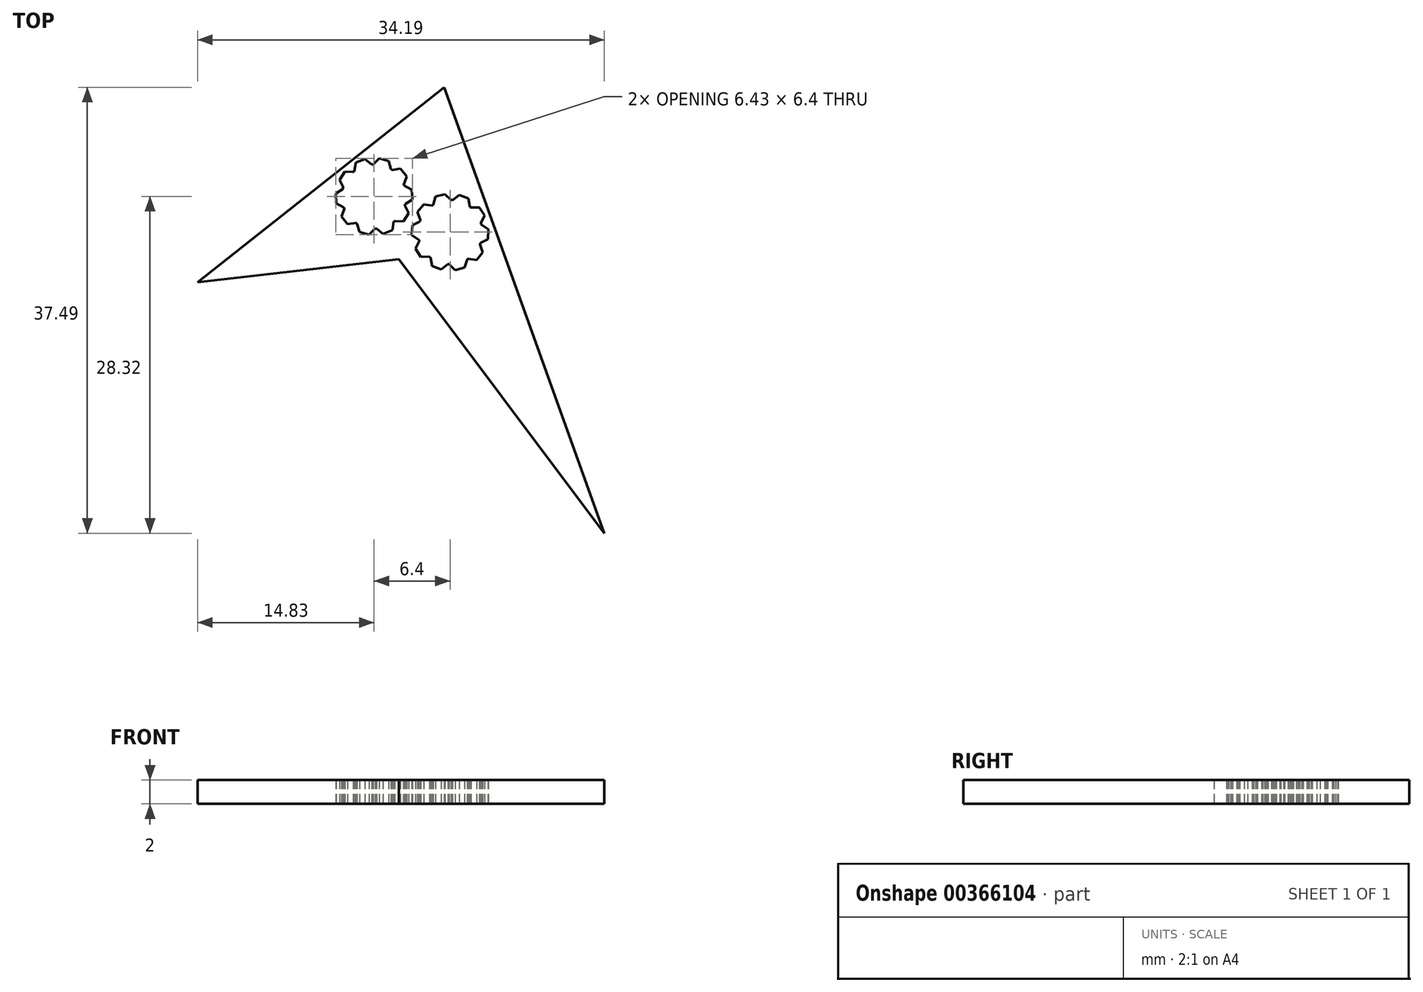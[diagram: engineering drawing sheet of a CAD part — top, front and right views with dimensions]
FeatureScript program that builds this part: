
annotation { "Feature Type Name" : "Feature", "Feature Type Description" : "" }
export const myFeature = defineFeature(function(context is Context, id is Id, definition is map)
    precondition{}
    {
        {
            var Q0;
            Q0=qCreatedBy(makeId("Top.planeOp"),FACE);
            var sketch = newSketch(context, id + "F0", { "sketchPlane" : qUnion([Q0])});
            skLineSegment(sketch, "E0", {"start": v(18, -24) * mm, "end": v(4, 15) * mm});
            skLineSegment(sketch, "E1", {"start": v(4, 15) * mm, "end": v(-17.5, -2) * mm});
            skLineSegment(sketch, "E2", {"start": v(-17.5, -2) * mm, "end": v(0, 0) * mm});
            skLineSegment(sketch, "E3", {"start": v(0, 0) * mm, "end": v(18, -24) * mm});
            skArc(sketch, "E4", {"start": v(-4.38, 6.27) * mm, "mid": v(-4.41, 6.15) * mm, "end": v(-4.45, 6.02) * mm, "construction": true});
            skLineSegment(sketch, "E5", {"start": v(-2, 8) * mm, "end": v(-1.51, 8.48) * mm});
            skLineSegment(sketch, "E6", {"start": v(-1.51, 8.48) * mm, "end": v(-0.93, 8.32) * mm});
            skLineSegment(sketch, "E7", {"start": v(-0.93, 8.32) * mm, "end": v(-0.75, 7.67) * mm});
            skLineSegment(sketch, "E8", {"start": v(-2, 5.5) * mm, "end": v(-1.22, 8.4) * mm, "construction": true});
            skLineSegment(sketch, "E9", {"start": v(-2, 8) * mm, "end": v(-2, 5.5) * mm, "construction": true});
            skLineSegment(sketch, "E10", {"start": v(-2, 5.5) * mm, "end": v(-0.75, 7.67) * mm, "construction": true});
            skLineSegment(sketch, "E11.1.0", {"start": v(-3.47, 7.52) * mm, "end": v(-3.36, 8.2) * mm});
            skLineSegment(sketch, "E11.1.1", {"start": v(-3.36, 8.2) * mm, "end": v(-2.8, 8.4) * mm});
            skLineSegment(sketch, "E11.1.2", {"start": v(-2.8, 8.4) * mm, "end": v(-2.26, 7.99) * mm});
            skLineSegment(sketch, "E11.2.0", {"start": v(-4.38, 6.27) * mm, "end": v(-4.68, 6.88) * mm});
            skLineSegment(sketch, "E11.2.1", {"start": v(-4.68, 6.88) * mm, "end": v(-4.35, 7.39) * mm});
            skLineSegment(sketch, "E11.2.2", {"start": v(-4.35, 7.39) * mm, "end": v(-3.67, 7.36) * mm});
            skLineSegment(sketch, "E11.3.0", {"start": v(-4.38, 4.73) * mm, "end": v(-4.98, 5.04) * mm});
            skLineSegment(sketch, "E11.3.1", {"start": v(-4.98, 5.04) * mm, "end": v(-5.01, 5.64) * mm});
            skLineSegment(sketch, "E11.3.2", {"start": v(-5.01, 5.64) * mm, "end": v(-4.45, 6.02) * mm});
            skLineSegment(sketch, "E11.4.0", {"start": v(-3.47, 3.48) * mm, "end": v(-4.14, 3.38) * mm});
            skLineSegment(sketch, "E11.4.1", {"start": v(-4.14, 3.38) * mm, "end": v(-4.52, 3.85) * mm});
            skLineSegment(sketch, "E11.4.2", {"start": v(-4.52, 3.85) * mm, "end": v(-4.28, 4.48) * mm});
            skLineSegment(sketch, "E11.5.0", {"start": v(-2, 3) * mm, "end": v(-2.49, 2.52) * mm});
            skLineSegment(sketch, "E11.5.1", {"start": v(-2.49, 2.52) * mm, "end": v(-3.07, 2.68) * mm});
            skLineSegment(sketch, "E11.5.2", {"start": v(-3.07, 2.68) * mm, "end": v(-3.25, 3.33) * mm});
            skLineSegment(sketch, "E11.6.0", {"start": v(-0.53, 3.48) * mm, "end": v(-0.64, 2.8) * mm});
            skLineSegment(sketch, "E11.6.1", {"start": v(-0.64, 2.8) * mm, "end": v(-1.2, 2.6) * mm});
            skLineSegment(sketch, "E11.6.2", {"start": v(-1.2, 2.6) * mm, "end": v(-1.74, 3.01) * mm});
            skLineSegment(sketch, "E11.7.0", {"start": v(0.38, 4.73) * mm, "end": v(0.68, 4.12) * mm});
            skLineSegment(sketch, "E11.7.1", {"start": v(0.68, 4.12) * mm, "end": v(0.35, 3.61) * mm});
            skLineSegment(sketch, "E11.7.2", {"start": v(0.35, 3.61) * mm, "end": v(-0.33, 3.64) * mm});
            skLineSegment(sketch, "E11.8.0", {"start": v(0.38, 6.27) * mm, "end": v(0.98, 5.96) * mm});
            skLineSegment(sketch, "E11.8.1", {"start": v(0.98, 5.96) * mm, "end": v(1.01, 5.36) * mm});
            skLineSegment(sketch, "E11.8.2", {"start": v(1.01, 5.36) * mm, "end": v(0.45, 4.98) * mm});
            skLineSegment(sketch, "E11.9.0", {"start": v(-0.53, 7.52) * mm, "end": v(0.14, 7.62) * mm});
            skLineSegment(sketch, "E11.9.1", {"start": v(0.14, 7.62) * mm, "end": v(0.52, 7.15) * mm});
            skLineSegment(sketch, "E11.9.2", {"start": v(0.52, 7.15) * mm, "end": v(0.28, 6.52) * mm});
            skArc(sketch, "E12", {"start": v(2.12, 3.52) * mm, "mid": v(2.07, 3.4) * mm, "end": v(2.02, 3.27) * mm, "construction": true});
            skLineSegment(sketch, "E13", {"start": v(3.15, 4.67) * mm, "end": v(3.33, 5.32) * mm});
            skLineSegment(sketch, "E14", {"start": v(3.33, 5.32) * mm, "end": v(3.91, 5.48) * mm});
            skLineSegment(sketch, "E15", {"start": v(3.91, 5.48) * mm, "end": v(4.4, 5) * mm});
            skLineSegment(sketch, "E16", {"start": v(4.4, 2.5) * mm, "end": v(3.62, 5.4) * mm, "construction": true});
            skLineSegment(sketch, "E17", {"start": v(3.15, 4.67) * mm, "end": v(4.4, 2.5) * mm, "construction": true});
            skLineSegment(sketch, "E18", {"start": v(4.4, 2.5) * mm, "end": v(4.4, 5) * mm, "construction": true});
            skLineSegment(sketch, "E19.1.0", {"start": v(2.12, 3.52) * mm, "end": v(1.88, 4.15) * mm});
            skLineSegment(sketch, "E19.1.1", {"start": v(1.88, 4.15) * mm, "end": v(2.26, 4.62) * mm});
            skLineSegment(sketch, "E19.1.2", {"start": v(2.26, 4.62) * mm, "end": v(2.93, 4.52) * mm});
            skLineSegment(sketch, "E19.2.0", {"start": v(1.95, 1.98) * mm, "end": v(1.39, 2.36) * mm});
            skLineSegment(sketch, "E19.2.1", {"start": v(1.39, 2.36) * mm, "end": v(1.42, 2.96) * mm});
            skLineSegment(sketch, "E19.2.2", {"start": v(1.42, 2.96) * mm, "end": v(2.02, 3.27) * mm});
            skLineSegment(sketch, "E19.3.0", {"start": v(2.73, 0.64) * mm, "end": v(2.05, 0.61) * mm});
            skLineSegment(sketch, "E19.3.1", {"start": v(2.05, 0.61) * mm, "end": v(1.72, 1.12) * mm});
            skLineSegment(sketch, "E19.3.2", {"start": v(1.72, 1.12) * mm, "end": v(2.02, 1.73) * mm});
            skLineSegment(sketch, "E19.4.0", {"start": v(4.14, 0.01) * mm, "end": v(3.6, -0.4) * mm});
            skLineSegment(sketch, "E19.4.1", {"start": v(3.6, -0.4) * mm, "end": v(3.04, -0.2) * mm});
            skLineSegment(sketch, "E19.4.2", {"start": v(3.04, -0.2) * mm, "end": v(2.93, 0.48) * mm});
            skLineSegment(sketch, "E19.5.0", {"start": v(5.65, 0.33) * mm, "end": v(5.47, -0.32) * mm});
            skLineSegment(sketch, "E19.5.1", {"start": v(5.47, -0.32) * mm, "end": v(4.89, -0.48) * mm});
            skLineSegment(sketch, "E19.5.2", {"start": v(4.89, -0.48) * mm, "end": v(4.4, 0) * mm});
            skLineSegment(sketch, "E19.6.0", {"start": v(6.68, 1.48) * mm, "end": v(6.92, 0.85) * mm});
            skLineSegment(sketch, "E19.6.1", {"start": v(6.92, 0.85) * mm, "end": v(6.54, 0.38) * mm});
            skLineSegment(sketch, "E19.6.2", {"start": v(6.54, 0.38) * mm, "end": v(5.87, 0.48) * mm});
            skLineSegment(sketch, "E19.7.0", {"start": v(6.85, 3.02) * mm, "end": v(7.41, 2.64) * mm});
            skLineSegment(sketch, "E19.7.1", {"start": v(7.41, 2.64) * mm, "end": v(7.38, 2.04) * mm});
            skLineSegment(sketch, "E19.7.2", {"start": v(7.38, 2.04) * mm, "end": v(6.78, 1.73) * mm});
            skLineSegment(sketch, "E19.8.0", {"start": v(6.07, 4.36) * mm, "end": v(6.75, 4.39) * mm});
            skLineSegment(sketch, "E19.8.1", {"start": v(6.75, 4.39) * mm, "end": v(7.08, 3.88) * mm});
            skLineSegment(sketch, "E19.8.2", {"start": v(7.08, 3.88) * mm, "end": v(6.78, 3.27) * mm});
            skLineSegment(sketch, "E19.9.0", {"start": v(4.66, 4.99) * mm, "end": v(5.2, 5.4) * mm});
            skLineSegment(sketch, "E19.9.1", {"start": v(5.2, 5.4) * mm, "end": v(5.76, 5.2) * mm});
            skLineSegment(sketch, "E19.9.2", {"start": v(5.76, 5.2) * mm, "end": v(5.87, 4.52) * mm});
            skArc(sketch, "E20", {"start": v(-4.38, 4.73) * mm, "mid": v(-4.33, 4.6) * mm, "end": v(-4.28, 4.48) * mm});
            skArc(sketch, "E21", {"start": v(2.12, 3.52) * mm, "mid": v(2.07, 3.4) * mm, "end": v(2.02, 3.27) * mm});
            skArc(sketch, "E22.trimOffspring", {"start": v(-4.38, 4.73) * mm, "mid": v(-4.33, 4.6) * mm, "end": v(-4.28, 4.48) * mm, "construction": true});
            skArc(sketch, "E23.trimOffspring", {"start": v(-3.47, 3.48) * mm, "mid": v(-3.36, 3.4) * mm, "end": v(-3.25, 3.33) * mm, "construction": true});
            skArc(sketch, "E24.trimOffspring", {"start": v(-4.38, 6.27) * mm, "mid": v(-4.41, 6.15) * mm, "end": v(-4.45, 6.02) * mm});
            skArc(sketch, "E25.trimOffspring", {"start": v(-3.47, 3.48) * mm, "mid": v(-3.36, 3.4) * mm, "end": v(-3.25, 3.33) * mm});
            skArc(sketch, "E26.trimOffspring", {"start": v(-2, 3) * mm, "mid": v(-1.87, 3) * mm, "end": v(-1.74, 3.01) * mm, "construction": true});
            skArc(sketch, "E27.trimOffspring", {"start": v(-2, 3) * mm, "mid": v(-1.87, 3) * mm, "end": v(-1.74, 3.01) * mm});
            skArc(sketch, "E28.trimOffspring", {"start": v(-0.53, 3.48) * mm, "mid": v(-0.43, 3.56) * mm, "end": v(-0.33, 3.64) * mm, "construction": true});
            skArc(sketch, "E29.trimOffspring", {"start": v(-0.53, 3.48) * mm, "mid": v(-0.43, 3.56) * mm, "end": v(-0.33, 3.64) * mm});
            skArc(sketch, "E30.trimOffspring", {"start": v(0.38, 4.73) * mm, "mid": v(0.41, 4.85) * mm, "end": v(0.45, 4.98) * mm, "construction": true});
            skArc(sketch, "E31.trimOffspring", {"start": v(0.38, 4.73) * mm, "mid": v(0.41, 4.85) * mm, "end": v(0.45, 4.98) * mm});
            skArc(sketch, "E32.trimOffspring", {"start": v(0.38, 6.27) * mm, "mid": v(0.33, 6.4) * mm, "end": v(0.28, 6.52) * mm, "construction": true});
            skArc(sketch, "E33.trimOffspring", {"start": v(0.38, 6.27) * mm, "mid": v(0.33, 6.4) * mm, "end": v(0.28, 6.52) * mm});
            skArc(sketch, "E34.trimOffspring", {"start": v(-0.53, 7.52) * mm, "mid": v(-0.64, 7.6) * mm, "end": v(-0.75, 7.67) * mm, "construction": true});
            skArc(sketch, "E35.trimOffspring", {"start": v(-0.53, 7.52) * mm, "mid": v(-0.64, 7.6) * mm, "end": v(-0.75, 7.67) * mm});
            skArc(sketch, "E36.trimOffspring", {"start": v(-3.47, 7.52) * mm, "mid": v(-3.57, 7.44) * mm, "end": v(-3.67, 7.36) * mm, "construction": true});
            skArc(sketch, "E37.trimOffspring", {"start": v(-3.47, 7.52) * mm, "mid": v(-3.57, 7.44) * mm, "end": v(-3.67, 7.36) * mm});
            skArc(sketch, "E38.trimOffspring", {"start": v(-2, 8) * mm, "mid": v(-2.13, 8) * mm, "end": v(-2.26, 7.99) * mm, "construction": true});
            skArc(sketch, "E39.trimOffspring", {"start": v(-2, 8) * mm, "mid": v(-2.13, 8) * mm, "end": v(-2.26, 7.99) * mm});
            skArc(sketch, "E40.trimOffspring", {"start": v(3.15, 4.67) * mm, "mid": v(3.04, 4.6) * mm, "end": v(2.93, 4.52) * mm, "construction": true});
            skArc(sketch, "E41.trimOffspring", {"start": v(3.15, 4.67) * mm, "mid": v(3.04, 4.6) * mm, "end": v(2.93, 4.52) * mm});
            skArc(sketch, "E42.trimOffspring", {"start": v(4.66, 4.99) * mm, "mid": v(4.53, 5) * mm, "end": v(4.4, 5) * mm, "construction": true});
            skArc(sketch, "E43.trimOffspring", {"start": v(4.66, 4.99) * mm, "mid": v(4.53, 5) * mm, "end": v(4.4, 5) * mm});
            skArc(sketch, "E44.trimOffspring", {"start": v(6.07, 4.36) * mm, "mid": v(5.97, 4.44) * mm, "end": v(5.87, 4.52) * mm, "construction": true});
            skArc(sketch, "E45.trimOffspring", {"start": v(6.07, 4.36) * mm, "mid": v(5.97, 4.44) * mm, "end": v(5.87, 4.52) * mm});
            skArc(sketch, "E46.trimOffspring", {"start": v(6.85, 3.02) * mm, "mid": v(6.81, 3.15) * mm, "end": v(6.78, 3.27) * mm, "construction": true});
            skArc(sketch, "E47.trimOffspring", {"start": v(6.85, 3.02) * mm, "mid": v(6.81, 3.15) * mm, "end": v(6.78, 3.27) * mm});
            skArc(sketch, "E48.trimOffspring", {"start": v(6.68, 1.48) * mm, "mid": v(6.73, 1.6) * mm, "end": v(6.78, 1.73) * mm, "construction": true});
            skArc(sketch, "E49.trimOffspring", {"start": v(6.68, 1.48) * mm, "mid": v(6.73, 1.6) * mm, "end": v(6.78, 1.73) * mm});
            skArc(sketch, "E50.trimOffspring", {"start": v(5.65, 0.33) * mm, "mid": v(5.76, 0.4) * mm, "end": v(5.87, 0.48) * mm, "construction": true});
            skArc(sketch, "E51.trimOffspring", {"start": v(5.65, 0.33) * mm, "mid": v(5.76, 0.4) * mm, "end": v(5.87, 0.48) * mm});
            skArc(sketch, "E52.trimOffspring", {"start": v(4.14, 0.01) * mm, "mid": v(4.27, 0) * mm, "end": v(4.4, 0) * mm, "construction": true});
            skArc(sketch, "E53.trimOffspring", {"start": v(4.14, 0.01) * mm, "mid": v(4.27, 0) * mm, "end": v(4.4, 0) * mm});
            skArc(sketch, "E54.trimOffspring", {"start": v(2.73, 0.64) * mm, "mid": v(2.83, 0.56) * mm, "end": v(2.93, 0.48) * mm, "construction": true});
            skArc(sketch, "E55.trimOffspring", {"start": v(2.73, 0.64) * mm, "mid": v(2.83, 0.56) * mm, "end": v(2.93, 0.48) * mm});
            skArc(sketch, "E56.trimOffspring", {"start": v(1.95, 1.98) * mm, "mid": v(1.99, 1.85) * mm, "end": v(2.02, 1.73) * mm, "construction": true});
            skArc(sketch, "E57.trimOffspring", {"start": v(1.95, 1.98) * mm, "mid": v(1.99, 1.85) * mm, "end": v(2.02, 1.73) * mm});
            skLineSegment(sketch, "E58.0", {"start": v(-4.54, 4.59) * mm, "end": v(-5.17, 4.92) * mm});
            skArc(sketch, "E58.1", {"start": v(-4.54, 4.59) * mm, "mid": v(-4.52, 4.53) * mm, "end": v(-4.5, 4.48) * mm});
            skLineSegment(sketch, "E58.2", {"start": v(-4.75, 3.8) * mm, "end": v(-4.5, 4.48) * mm});
            skLineSegment(sketch, "E58.3", {"start": v(-4.23, 3.16) * mm, "end": v(-4.75, 3.8) * mm});
            skLineSegment(sketch, "E58.4", {"start": v(-3.52, 3.27) * mm, "end": v(-4.23, 3.16) * mm});
            skArc(sketch, "E58.5", {"start": v(-3.52, 3.27) * mm, "mid": v(-3.47, 3.24) * mm, "end": v(-3.42, 3.2) * mm});
            skLineSegment(sketch, "E58.6", {"start": v(-3.23, 2.52) * mm, "end": v(-3.42, 3.2) * mm});
            skLineSegment(sketch, "E58.7", {"start": v(-2.43, 2.3) * mm, "end": v(-3.23, 2.52) * mm});
            skLineSegment(sketch, "E58.8", {"start": v(-1.92, 2.8) * mm, "end": v(-2.43, 2.3) * mm});
            skArc(sketch, "E58.9", {"start": v(-1.92, 2.8) * mm, "mid": v(-1.86, 2.8) * mm, "end": v(-1.8, 2.8) * mm});
            skLineSegment(sketch, "E58.10", {"start": v(-1.24, 2.36) * mm, "end": v(-1.8, 2.8) * mm});
            skLineSegment(sketch, "E58.11", {"start": v(-5.17, 4.92) * mm, "end": v(-5.22, 5.75) * mm});
            skLineSegment(sketch, "E58.12", {"start": v(-0.47, 2.66) * mm, "end": v(-1.24, 2.36) * mm});
            skLineSegment(sketch, "E58.13", {"start": v(-0.35, 3.37) * mm, "end": v(-0.47, 2.66) * mm});
            skArc(sketch, "E58.14", {"start": v(-0.35, 3.37) * mm, "mid": v(-0.3, 3.4) * mm, "end": v(-0.26, 3.44) * mm});
            skLineSegment(sketch, "E58.15", {"start": v(0.46, 3.41) * mm, "end": v(-0.26, 3.44) * mm});
            skLineSegment(sketch, "E58.16", {"start": v(0.9, 4.1) * mm, "end": v(0.46, 3.41) * mm});
            skLineSegment(sketch, "E58.17", {"start": v(0.6, 4.74) * mm, "end": v(0.9, 4.1) * mm});
            skArc(sketch, "E58.18", {"start": v(-2.08, 8.2) * mm, "mid": v(-2.14, 8.2) * mm, "end": v(-2.2, 8.2) * mm});
            skLineSegment(sketch, "E58.19", {"start": v(-2.76, 8.64) * mm, "end": v(-2.2, 8.2) * mm});
            skLineSegment(sketch, "E58.20", {"start": v(-3.53, 8.34) * mm, "end": v(-2.76, 8.64) * mm});
            skLineSegment(sketch, "E58.21", {"start": v(-3.65, 7.63) * mm, "end": v(-3.53, 8.34) * mm});
            skArc(sketch, "E58.22", {"start": v(-3.65, 7.63) * mm, "mid": v(-3.7, 7.6) * mm, "end": v(-3.74, 7.56) * mm});
            skLineSegment(sketch, "E58.23", {"start": v(-4.46, 7.59) * mm, "end": v(-3.74, 7.56) * mm});
            skLineSegment(sketch, "E58.24", {"start": v(-5.22, 5.75) * mm, "end": v(-4.62, 6.14) * mm});
            skArc(sketch, "E58.25", {"start": v(-4.6, 6.26) * mm, "mid": v(-4.6, 6.2) * mm, "end": v(-4.62, 6.14) * mm});
            skLineSegment(sketch, "E58.26", {"start": v(-4.6, 6.26) * mm, "end": v(-4.9, 6.9) * mm});
            skLineSegment(sketch, "E58.27", {"start": v(-4.9, 6.9) * mm, "end": v(-4.46, 7.59) * mm});
            skLineSegment(sketch, "E58.28", {"start": v(-2.08, 8.2) * mm, "end": v(-1.57, 8.7) * mm});
            skLineSegment(sketch, "E58.29", {"start": v(-1.57, 8.7) * mm, "end": v(-0.77, 8.48) * mm});
            skLineSegment(sketch, "E58.30", {"start": v(-0.77, 8.48) * mm, "end": v(-0.58, 7.8) * mm});
            skArc(sketch, "E58.31", {"start": v(-0.48, 7.73) * mm, "mid": v(-0.53, 7.76) * mm, "end": v(-0.58, 7.8) * mm});
            skLineSegment(sketch, "E58.32", {"start": v(-0.48, 7.73) * mm, "end": v(0.23, 7.84) * mm});
            skLineSegment(sketch, "E58.33", {"start": v(0.23, 7.84) * mm, "end": v(0.75, 7.2) * mm});
            skLineSegment(sketch, "E58.34", {"start": v(0.75, 7.2) * mm, "end": v(0.5, 6.52) * mm});
            skArc(sketch, "E58.35", {"start": v(0.54, 6.41) * mm, "mid": v(0.52, 6.47) * mm, "end": v(0.5, 6.52) * mm});
            skLineSegment(sketch, "E58.36", {"start": v(0.54, 6.41) * mm, "end": v(1.17, 6.08) * mm});
            skLineSegment(sketch, "E58.37", {"start": v(1.17, 6.08) * mm, "end": v(1.22, 5.25) * mm});
            skLineSegment(sketch, "E58.38", {"start": v(1.22, 5.25) * mm, "end": v(0.62, 4.86) * mm});
            skArc(sketch, "E58.39", {"start": v(0.6, 4.74) * mm, "mid": v(0.6, 4.8) * mm, "end": v(0.62, 4.86) * mm});
            skLineSegment(sketch, "E59.0", {"start": v(2.98, 4.8) * mm, "end": v(3.17, 5.48) * mm});
            skArc(sketch, "E59.1", {"start": v(2.98, 4.8) * mm, "mid": v(2.93, 4.76) * mm, "end": v(2.88, 4.73) * mm});
            skLineSegment(sketch, "E59.2", {"start": v(2.17, 4.84) * mm, "end": v(2.88, 4.73) * mm});
            skLineSegment(sketch, "E59.3", {"start": v(1.65, 4.2) * mm, "end": v(2.17, 4.84) * mm});
            skLineSegment(sketch, "E59.4", {"start": v(1.9, 3.52) * mm, "end": v(1.65, 4.2) * mm});
            skArc(sketch, "E59.5", {"start": v(1.9, 3.52) * mm, "mid": v(1.88, 3.47) * mm, "end": v(1.86, 3.41) * mm});
            skLineSegment(sketch, "E59.6", {"start": v(1.23, 3.08) * mm, "end": v(1.86, 3.41) * mm});
            skLineSegment(sketch, "E59.7", {"start": v(1.18, 2.25) * mm, "end": v(1.23, 3.08) * mm});
            skLineSegment(sketch, "E59.8", {"start": v(1.78, 1.86) * mm, "end": v(1.18, 2.25) * mm});
            skArc(sketch, "E59.9", {"start": v(1.78, 1.86) * mm, "mid": v(1.8, 1.8) * mm, "end": v(1.8, 1.74) * mm});
            skLineSegment(sketch, "E59.10", {"start": v(1.5, 1.1) * mm, "end": v(1.8, 1.74) * mm});
            skLineSegment(sketch, "E59.11", {"start": v(3.17, 5.48) * mm, "end": v(3.97, 5.7) * mm});
            skLineSegment(sketch, "E59.12", {"start": v(1.94, 0.41) * mm, "end": v(1.5, 1.1) * mm});
            skLineSegment(sketch, "E59.13", {"start": v(2.66, 0.44) * mm, "end": v(1.94, 0.41) * mm});
            skArc(sketch, "E59.14", {"start": v(2.66, 0.44) * mm, "mid": v(2.7, 0.4) * mm, "end": v(2.75, 0.37) * mm});
            skLineSegment(sketch, "E59.15", {"start": v(2.87, -0.34) * mm, "end": v(2.75, 0.37) * mm});
            skLineSegment(sketch, "E59.16", {"start": v(3.64, -0.64) * mm, "end": v(2.87, -0.34) * mm});
            skLineSegment(sketch, "E59.17", {"start": v(4.2, -0.2) * mm, "end": v(3.64, -0.64) * mm});
            skArc(sketch, "E59.18", {"start": v(7.02, 3.14) * mm, "mid": v(7, 3.2) * mm, "end": v(7, 3.26) * mm});
            skLineSegment(sketch, "E59.19", {"start": v(7.3, 3.9) * mm, "end": v(7, 3.26) * mm});
            skLineSegment(sketch, "E59.20", {"start": v(6.86, 4.59) * mm, "end": v(7.3, 3.9) * mm});
            skLineSegment(sketch, "E59.21", {"start": v(6.14, 4.56) * mm, "end": v(6.86, 4.59) * mm});
            skArc(sketch, "E59.22", {"start": v(6.14, 4.56) * mm, "mid": v(6.1, 4.6) * mm, "end": v(6.05, 4.63) * mm});
            skLineSegment(sketch, "E59.23", {"start": v(5.93, 5.34) * mm, "end": v(6.05, 4.63) * mm});
            skLineSegment(sketch, "E59.24", {"start": v(3.97, 5.7) * mm, "end": v(4.48, 5.2) * mm});
            skArc(sketch, "E59.25", {"start": v(4.6, 5.2) * mm, "mid": v(4.54, 5.2) * mm, "end": v(4.48, 5.2) * mm});
            skLineSegment(sketch, "E59.26", {"start": v(4.6, 5.2) * mm, "end": v(5.16, 5.64) * mm});
            skLineSegment(sketch, "E59.27", {"start": v(5.16, 5.64) * mm, "end": v(5.93, 5.34) * mm});
            skLineSegment(sketch, "E59.28", {"start": v(7.02, 3.14) * mm, "end": v(7.62, 2.75) * mm});
            skLineSegment(sketch, "E59.29", {"start": v(7.62, 2.75) * mm, "end": v(7.57, 1.92) * mm});
            skLineSegment(sketch, "E59.30", {"start": v(7.57, 1.92) * mm, "end": v(6.94, 1.59) * mm});
            skArc(sketch, "E59.31", {"start": v(6.9, 1.48) * mm, "mid": v(6.92, 1.53) * mm, "end": v(6.94, 1.59) * mm});
            skLineSegment(sketch, "E59.32", {"start": v(6.9, 1.48) * mm, "end": v(7.15, 0.8) * mm});
            skLineSegment(sketch, "E59.33", {"start": v(7.15, 0.8) * mm, "end": v(6.63, 0.16) * mm});
            skLineSegment(sketch, "E59.34", {"start": v(6.63, 0.16) * mm, "end": v(5.92, 0.27) * mm});
            skArc(sketch, "E59.35", {"start": v(5.82, 0.2) * mm, "mid": v(5.87, 0.24) * mm, "end": v(5.92, 0.27) * mm});
            skLineSegment(sketch, "E59.36", {"start": v(5.82, 0.2) * mm, "end": v(5.63, -0.48) * mm});
            skLineSegment(sketch, "E59.37", {"start": v(5.63, -0.48) * mm, "end": v(4.83, -0.7) * mm});
            skLineSegment(sketch, "E59.38", {"start": v(4.83, -0.7) * mm, "end": v(4.32, -0.2) * mm});
            skArc(sketch, "E59.39", {"start": v(4.2, -0.2) * mm, "mid": v(4.26, -0.2) * mm, "end": v(4.32, -0.2) * mm});
            skLineSegment(sketch, "E60.0", {"start": v(3.9, 14.67) * mm, "end": v(-16.83, -1.72) * mm});
            skLineSegment(sketch, "E60.1", {"start": v(17.36, -22.82) * mm, "end": v(3.9, 14.67) * mm});
            skLineSegment(sketch, "E60.2", {"start": v(0.1, 0.21) * mm, "end": v(17.36, -22.82) * mm});
            skLineSegment(sketch, "E60.3", {"start": v(-16.83, -1.72) * mm, "end": v(0.1, 0.21) * mm});
            skSolve(sketch);
        }
        {
            var Q0;
            Q0=makeQuery(id+"F0.imprint","IMPRINT",FACE,{"disambiguationData":[TD([[makeQuery(id+"F0.imprint","IMPRINT",EDGE,{"derivedFrom":sQuery(id+"F0.wireOp",EDGE,"E58.0")}),1.0]])]});
            extrude(context, id + "F1", {"entities" : qUnion([Q0]), "depth" : 2 * mm});
        }
    });
